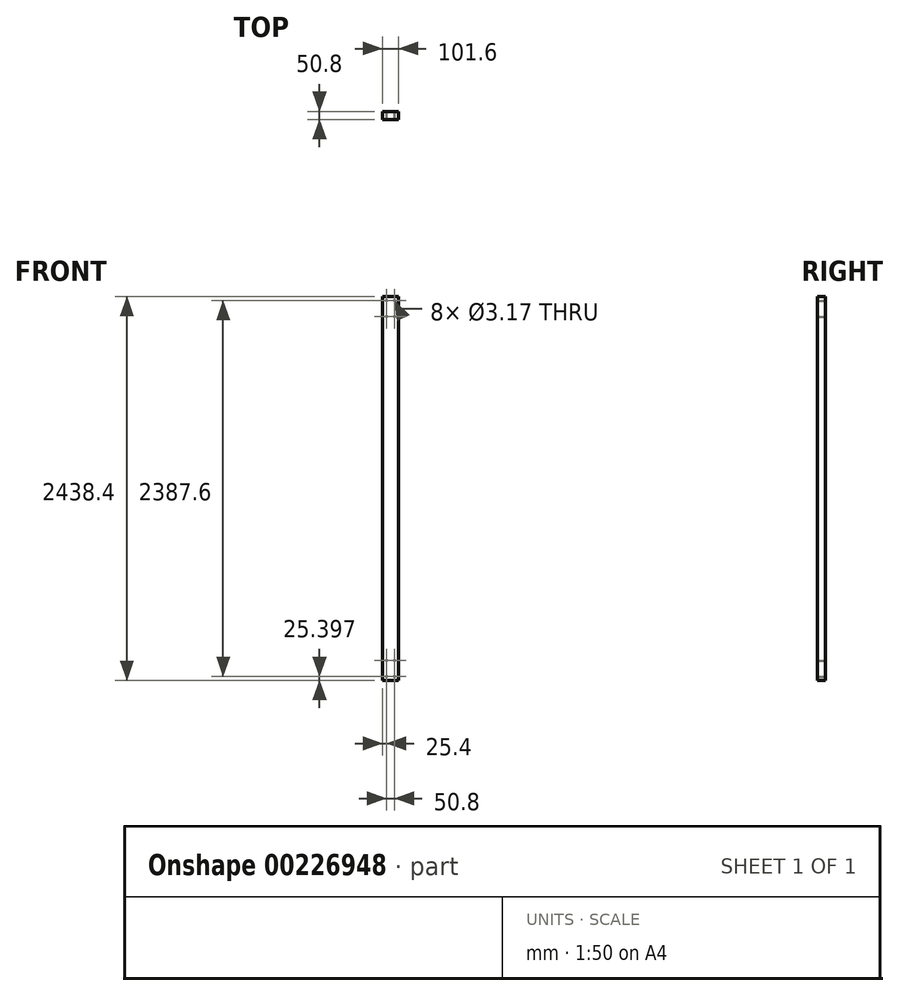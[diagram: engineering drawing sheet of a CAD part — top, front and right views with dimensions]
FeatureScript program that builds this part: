
annotation { "Feature Type Name" : "Feature", "Feature Type Description" : "" }
export const myFeature = defineFeature(function(context is Context, id is Id, definition is map)
    precondition{}
    {
        {
            var Q0;
            Q0=qCreatedBy(makeId("Front.planeOp"),FACE);
            var sketch = newSketch(context, id + "F0", { "sketchPlane" : qUnion([Q0])});
            skLineSegment(sketch, "E0", {"start": v(-76.2, 1212.3) * mm, "end": v(25.4, 1212.3) * mm});
            skLineSegment(sketch, "E1", {"start": v(25.4, -1226.1) * mm, "end": v(25.4, 1212.3) * mm});
            skLineSegment(sketch, "E2", {"start": v(-76.2, 1212.3) * mm, "end": v(-76.2, -1226.1) * mm});
            skLineSegment(sketch, "E3", {"start": v(25.4, -1226.1) * mm, "end": v(-76.2, -1226.1) * mm});
            skCircle(sketch, "E4", {"center": v(-50.8, 1186.9) * mm, "radius": 1.59 * mm});
            skCircle(sketch, "E5", {"center": v(0, 1186.9) * mm, "radius": 1.59 * mm});
            skCircle(sketch, "E6", {"center": v(-50.8, 1085.3) * mm, "radius": 1.59 * mm});
            skCircle(sketch, "E7", {"center": v(0, 1085.3) * mm, "radius": 1.59 * mm});
            skCircle(sketch, "E8", {"center": v(-50.8, -1200.7) * mm, "radius": 1.59 * mm});
            skCircle(sketch, "E9", {"center": v(0, -1200.7) * mm, "radius": 1.59 * mm});
            skCircle(sketch, "E10", {"center": v(0, -1099.1) * mm, "radius": 1.59 * mm});
            skCircle(sketch, "E11", {"center": v(-50.8, -1099.1) * mm, "radius": 1.59 * mm});
            skSolve(sketch);
        }
        {
            var Q0;
            Q0 = qSketchRegion(id + "F0", true);
            extrude(context, id + "F1", {"entities" : qUnion([Q0]), "depth" : 50.8 * mm});
        }
    });
